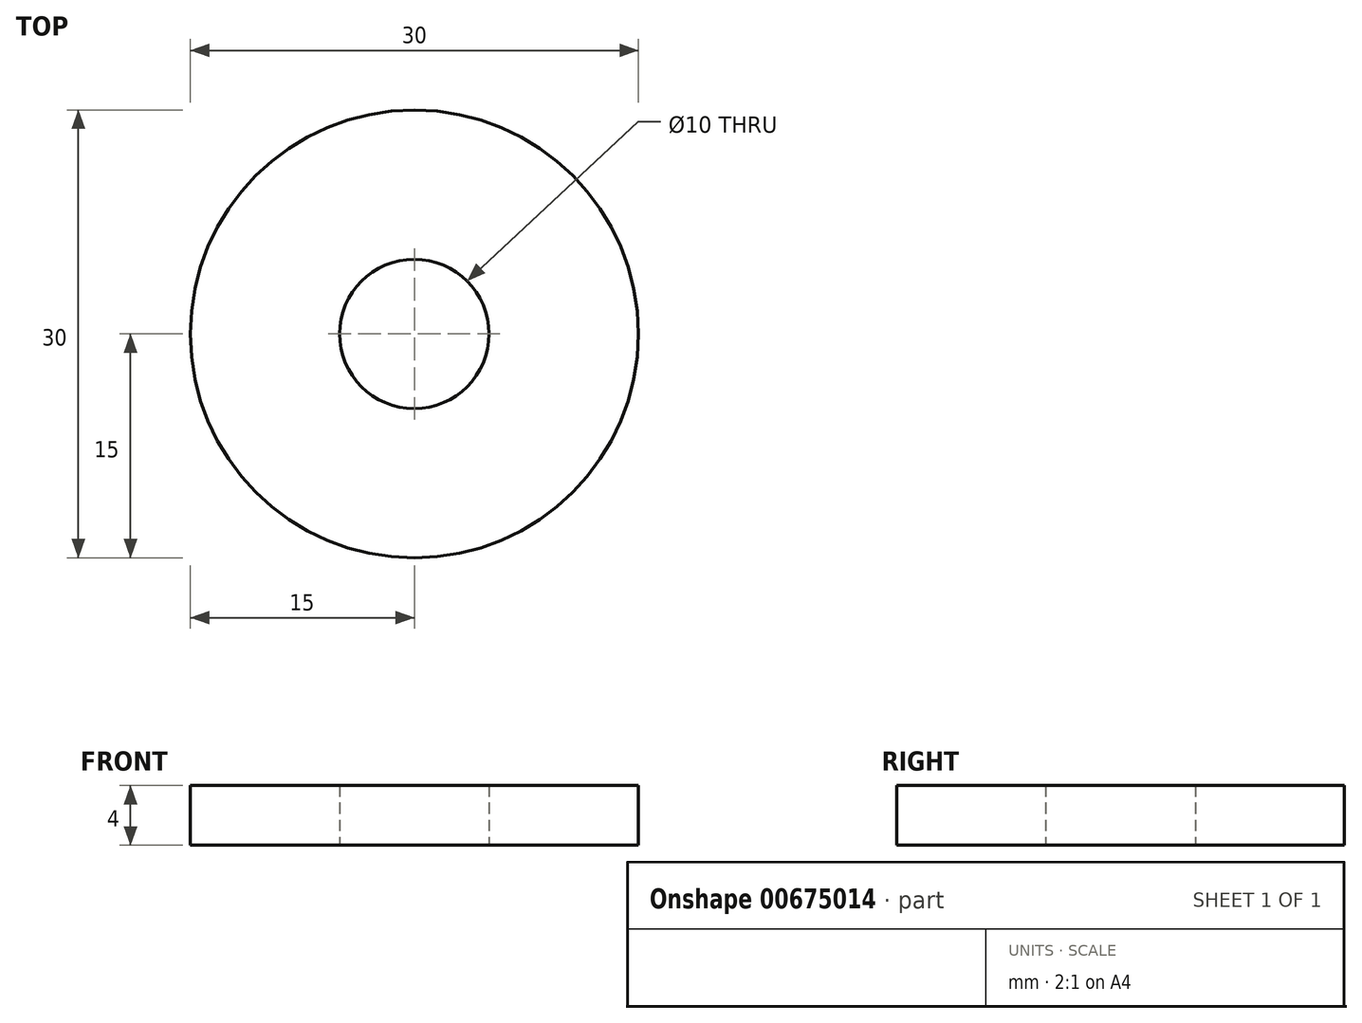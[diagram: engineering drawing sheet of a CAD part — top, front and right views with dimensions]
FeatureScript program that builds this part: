
annotation { "Feature Type Name" : "Feature", "Feature Type Description" : "" }
export const myFeature = defineFeature(function(context is Context, id is Id, definition is map)
    precondition{}
    {
        {
            var Q0;
            Q0=qCreatedBy(makeId("Top.planeOp"),FACE);
            var sketch = newSketch(context, id + "F0", { "sketchPlane" : qUnion([Q0])});
            skCircle(sketch, "E0", {"center": v(0, 0) * mm, "radius": 15 * mm});
            skCircle(sketch, "E1", {"center": v(0, 0) * mm, "radius": 5 * mm});
            skSolve(sketch);
        }
        {
            var Q0;
            Q0=makeQuery(id+"F0.imprint","IMPRINT",FACE,{"disambiguationData":[TD([[makeQuery(id+"F0.imprint","IMPRINT",EDGE,{"derivedFrom":sQuery(id+"F0.wireOp",EDGE,"E0")}),1.0]])]});
            extrude(context, id + "F1", {"entities" : qUnion([Q0]), "depth" : 4 * mm, "offsetDistance" : 25 * mm});
        }
    });
